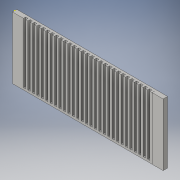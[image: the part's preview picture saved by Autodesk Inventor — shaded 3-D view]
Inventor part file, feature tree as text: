
AUTODESK INVENTOR PART (.ipt)
format: ipt  version: 2016 (Build 200138000, 138)  size: 518,656 bytes
history: native  units: in
note: dims shown in document units (in); Inventor stores cm internally (conversion verified against a paired STEP export)
features: sketch x35, extrude x34, pattern_linear x13
ambient origin geometry x8: Origin, YZ Plane, XZ Plane, XY Plane, X Axis, Y Axis, Z Axis, Center Point
bodies: Solid1 (feature_tree)
feature tree (82):
  extrude  "Extrusion1"  Depth=3.5in
  extrude  "Extrusion2"  Depth=0.625in
  extrude  "Extrusion3"  Depth=0.125in TaperAngle=0.0deg
  extrude  "Extrusion4"  Depth=0.125in
  extrude  "Extrusion5"  Depth=0.125in
  sketch  "Sketch6"  dims[d13=3.5in d14=0.125in d15=0.0in]
  extrude  "Extrusion6"  Depth=0.125in TaperAngle=0.0deg
  extrude  "Extrusion7"  Depth=0.125in
  extrude  "Extrusion8"  Depth=0.125in
  extrude  "Extrusion9"  Depth=0.125in TaperAngle=0.0deg
  extrude  "Extrusion10"  Depth=0.125in
  extrude  "Extrusion11"  Depth=0.125in
  extrude  "Extrusion12"  Depth=0.125in TaperAngle=0.0deg
  extrude  "Extrusion13"  Depth=3.5in
  extrude  "Extrusion14"  Depth=0.125in
  extrude  "Extrusion15"  Depth=0.125in TaperAngle=0.0deg
  extrude  "Extrusion16"  Depth=3.5in
  extrude  "Extrusion17"  Depth=0.125in
  extrude  "Extrusion18"  Depth=0.125in TaperAngle=0.0deg
  extrude  "Extrusion19"  Depth=3.5in
  extrude  "Extrusion20"  Depth=0.125in
  extrude  "Extrusion21"  Depth=0.125in TaperAngle=0.0deg
  extrude  "Extrusion22"  Depth=3.5in
  extrude  "Extrusion23"  Depth=0.125in
  extrude  "Extrusion24"  Depth=0.125in TaperAngle=0.0deg
  extrude  "Extrusion25"  Depth=3.5in
  extrude  "Extrusion26"  Depth=0.125in
  extrude  "Extrusion27"  Depth=0.125in TaperAngle=0.0deg
  extrude  "Extrusion28"  Depth=3.5in
  extrude  "Extrusion29"  Depth=0.125in
  extrude  "Extrusion30"  Depth=0.125in TaperAngle=0.0deg
  extrude  "Extrusion31"  Depth=3.5in
  extrude  "Extrusion32"  Depth=0.125in
  extrude  "Extrusion33"  Depth=0.125in TaperAngle=0.0deg
  extrude  "Extrusion34"  Depth=3.5in
  pattern_linear  "Rectangular Pattern1"  Spacing1=0.125in  [1 undecoded]
  pattern_linear  "Rectangular Pattern2"  Spacing1=0.125in  [1 undecoded]
  pattern_linear  "Rectangular Pattern3"  Spacing1=0.125in  [1 undecoded]
  pattern_linear  "Rectangular Pattern4"  Spacing1=0.125in  [1 undecoded]
  pattern_linear  "Rectangular Pattern5"  Spacing1=3.5in  [1 undecoded]
  pattern_linear  "Rectangular Pattern6"  Spacing1=0.125in  [1 undecoded]
  pattern_linear  "Rectangular Pattern7"  Spacing1=0.125in  [1 undecoded]
  pattern_linear  "Rectangular Pattern8"  Spacing1=0.125in  [1 undecoded]
  pattern_linear  "Rectangular Pattern9"  Spacing1=0.125in  [1 undecoded]
  pattern_linear  "Rectangular Pattern10"  Spacing1=0.125in  [1 undecoded]
  pattern_linear  "Rectangular Pattern11"  Spacing1=3.5in  [1 undecoded]
  pattern_linear  "Rectangular Pattern12"  Spacing1=0.125in  [1 undecoded]
  pattern_linear  "Rectangular Pattern13"  Spacing1=0.125in  [1 undecoded]
  sketch  "Sketch1"  dims[d0=8.5in d1=3.5in]
  sketch  "Sketch2"  dims[d2=0.125in d3=0.0in d4=0.625in]
  sketch  "Sketch3"  dims[d5=3.5in d6=0.125in d7=0.0in]
  sketch  "Sketch4"  dims[d8=0.125in d9=0.125in]
  sketch  "Sketch5"  dims[d10=0.125in d11=0.0in d12=0.125in]
  sketch  "Sketch7"  dims[d16=0.125in d17=0.125in]
  sketch  "Sketch8"  dims[d18=0.125in d19=0.0in d20=0.125in]
  sketch  "Sketch9"  dims[d21=3.5in d22=0.125in d23=0.0in]
  sketch  "Sketch10"  dims[d24=0.125in d25=0.125in]
  sketch  "Sketch11"  dims[d26=0.125in d27=0.0in d28=0.125in]
  sketch  "Sketch12"  dims[d29=3.5in d30=0.125in d31=0.0in]
  sketch  "Sketch13"  dims[d32=0.625in d33=3.5in]
  sketch  "Sketch14"  dims[d34=0.125in d35=0.0in d36=0.125in]
  sketch  "Sketch15"  dims[d37=0.125in d38=0.125in d39=0.0in]
  sketch  "Sketch16"  dims[d40=0.125in d41=3.5in]
  sketch  "Sketch17"  dims[d42=0.125in d43=0.0in d44=0.125in]
  sketch  "Sketch18"  dims[d45=0.125in d46=0.125in d47=0.0in]
  sketch  "Sketch19"  dims[d48=0.125in d49=3.5in]
  sketch  "Sketch20"  dims[d50=0.125in d51=0.0in d52=0.125in]
  sketch  "Sketch21"  dims[d53=0.125in d54=0.125in d55=0.0in]
  sketch  "Sketch22"  dims[d56=0.125in d57=3.5in]
  sketch  "Sketch23"  dims[d58=0.125in d59=0.0in d60=0.125in]
  sketch  "Sketch24"  dims[d61=0.125in d62=0.125in d63=0.0in]
  sketch  "Sketch25"  dims[d64=0.125in d65=3.5in]
  sketch  "Sketch26"  dims[d66=0.125in d67=0.0in d68=0.125in]
  sketch  "Sketch27"  dims[d69=0.125in d70=0.125in d71=0.0in]
  sketch  "Sketch28"  dims[d72=0.125in d73=3.5in]
  sketch  "Sketch29"  dims[d74=0.125in d75=0.0in d76=0.125in]
  sketch  "Sketch30"  dims[d77=0.125in d78=0.125in d79=0.0in]
  sketch  "Sketch31"  dims[d80=0.125in d81=3.5in]
  sketch  "Sketch32"  dims[d82=0.125in d83=0.0in d84=0.125in]
  sketch  "Sketch33"  dims[d85=0.125in d86=0.125in d87=0.0in]
  sketch  "Sketch34"  dims[d88=0.125in d89=3.5in]
  sketch  "Sketch35"  dims[d90=0.125in d91=0.0in d92=0.125in d93=0.125in d94=0.125in d95=0.0in d96=0.125in d97=3.5in d98=0.125in d99=0.0in d100=0.125in d101=0.125in d102=0.125in d103=0.0in d104=0.125in d105=3.5in d106=0.125in d107=0.0in d108=0.125in d109=0.125in d110=0.125in d111=0.0in d112=0.125in d113=3.5in d114=0.125in d115=0.0in d116=0.125in d117=0.125in d118=0.0in d119=0.125in d120=3.5in d121=0.125in d122=0.0in d123=0.125in d124=0.125in d125=0.125in d126=0.0in d127=0.125in d128=3.5in d129=0.125in d130=0.0in d131=0.125in d132=0.125in d133=0.125in d134=0.0in d135=0.7874in d137=0.25in d138=0.7874in d140=0.25in d141=0.7874in d143=0.5in d144=0.7874in d146=0.5in d147=0.7874in d149=1.0in d150=0.7874in d152=1.0in d153=0.7874in d155=2.25in d156=0.7874in d158=3.0in d159=0.7874in d161=2.0in d162=0.7874in d164=3.5in d165=0.7874in d167=4.5in d168=0.7874in d170=2.5in d171=0.7874in d173=4.25in]
note: 13 required parameter values undecoded (feature->parameter linkage not recoverable at this tier; creation-order binding heuristic only, values carry confidence <= 0.55)
